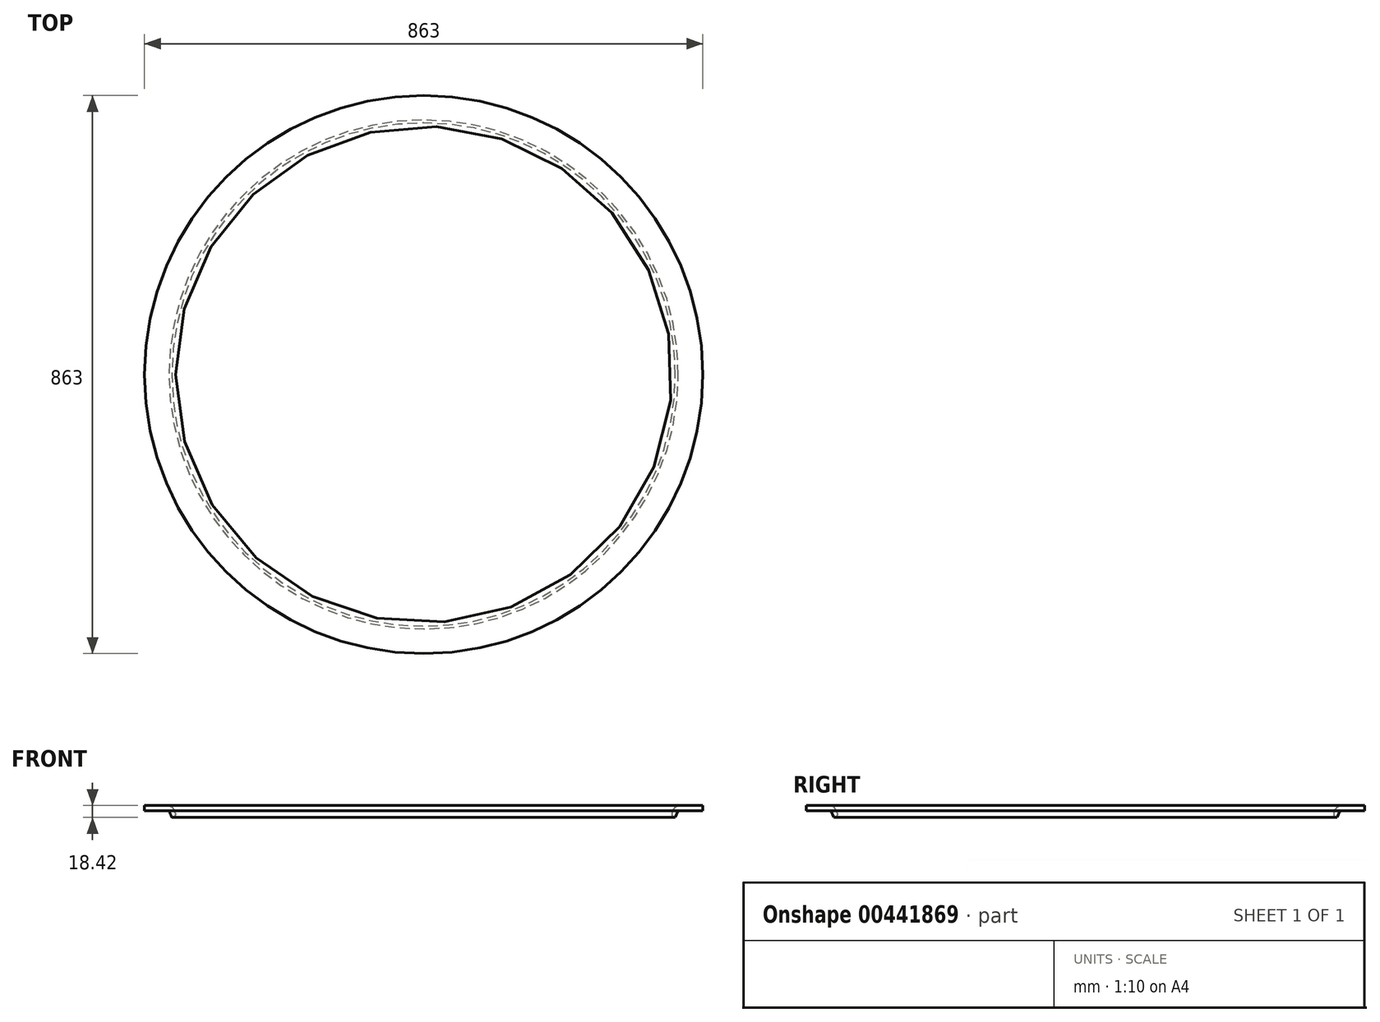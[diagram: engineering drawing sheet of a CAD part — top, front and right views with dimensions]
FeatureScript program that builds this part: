
annotation { "Feature Type Name" : "Feature", "Feature Type Description" : "" }
export const myFeature = defineFeature(function(context is Context, id is Id, definition is map)
    precondition{}
    {
        {
            var Q0;
            Q0=qCreatedBy(makeId("Front.planeOp"),FACE);
            var sketch = newSketch(context, id + "F0", { "sketchPlane" : qUnion([Q0])});
            skLineSegment(sketch, "E0.bottom", {"start": v(0, 0) * mm, "end": v(38, 0) * mm});
            skLineSegment(sketch, "E0.top", {"start": v(0, 8) * mm, "end": v(35.99, 8) * mm});
            skLineSegment(sketch, "E0.left", {"start": v(0, 0) * mm, "end": v(0, 8) * mm});
            skLineSegment(sketch, "E0.right", {"start": v(46, 0) * mm, "end": v(45.2, 1.9) * mm});
            skLineSegment(sketch, "E1.bottom", {"start": v(42.86, -10.42) * mm, "end": v(42.41, -10.42) * mm});
            skLineSegment(sketch, "E1.left", {"start": v(47.47, -3.46) * mm, "end": v(46, 0) * mm});
            skLineSegment(sketch, "E1.right", {"start": v(42.41, -10.42) * mm, "end": v(38, 0) * mm});
            skPoint(sketch, "E2.visualSharp", {"position": v(42.61, 8) * mm});
            skArc(sketch, "E2.filletArc", {"start": v(45.2, 1.9) * mm, "mid": v(41.5, 6.34) * mm, "end": v(35.99, 8) * mm});
            skPoint(sketch, "E3.visualSharp", {"position": v(50.41, -10.42) * mm});
            skArc(sketch, "E3.filletArc", {"start": v(42.86, -10.42) * mm, "mid": v(47.03, -8.18) * mm, "end": v(47.47, -3.46) * mm});
            skSolve(sketch);
        }
        {
            var Q0;
            Q0=qCreatedBy(makeId("Top.planeOp"),FACE);
            var sketch = newSketch(context, id + "F1", { "sketchPlane" : qUnion([Q0])});
            skCircle(sketch, "E4", {"center": v(431.5, 0) * mm, "radius": 412.5 * mm});
            skSolve(sketch);
        }
        {
            var Q0;
            Q0 = qSketchRegion(id + "F0", true);
            var Q1;
            Q1 = qConstructionFilter(qBodyType(qCreatedBy(id + "F1" ,EDGE), BodyType.WIRE), ConstructionObject.NO);
            sweep(context, id + "F2", {"profiles" : qUnion([Q0]), "path" : qUnion([Q1])});
        }
    });
